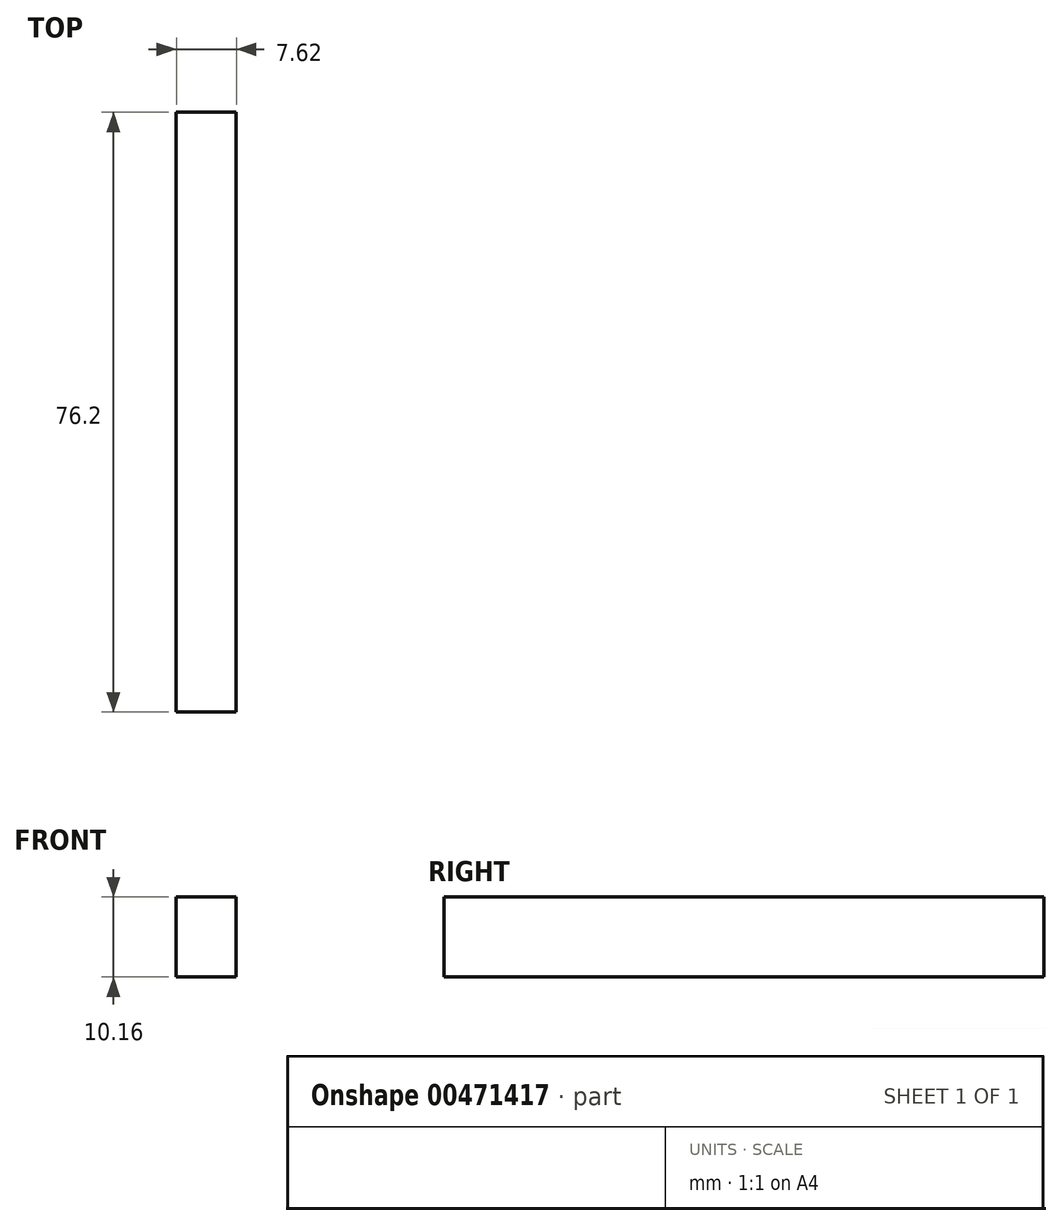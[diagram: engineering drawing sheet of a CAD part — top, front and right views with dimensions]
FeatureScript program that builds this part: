
annotation { "Feature Type Name" : "Feature", "Feature Type Description" : "" }
export const myFeature = defineFeature(function(context is Context, id is Id, definition is map)
    precondition{}
    {
        {
            var Q0;
            Q0=qCreatedBy(makeId("Front.planeOp"),FACE);
            var sketch = newSketch(context, id + "F0", { "sketchPlane" : qUnion([Q0])});
            skLineSegment(sketch, "E0.bottom", {"start": v(-3.68, 8.02) * mm, "end": v(3.94, 8.02) * mm});
            skLineSegment(sketch, "E0.top", {"start": v(-3.68, -2.14) * mm, "end": v(3.94, -2.14) * mm});
            skLineSegment(sketch, "E0.left", {"start": v(-3.68, 8.02) * mm, "end": v(-3.68, -2.14) * mm});
            skLineSegment(sketch, "E0.right", {"start": v(3.94, 8.02) * mm, "end": v(3.94, -2.14) * mm});
            skSolve(sketch);
        }
        {
            var Q0;
            Q0=makeQuery(id+"F0.imprint","IMPRINT",FACE,{"disambiguationData":[TD([[makeQuery(id+"F0.imprint","IMPRINT",EDGE,{"derivedFrom":sQuery(id+"F0.wireOp",EDGE,"E0.bottom")}),-1.0]])]});
            extrude(context, id + "F1", {"entities" : qUnion([Q0]), "depth" : 76.2 * mm});
        }
    });
